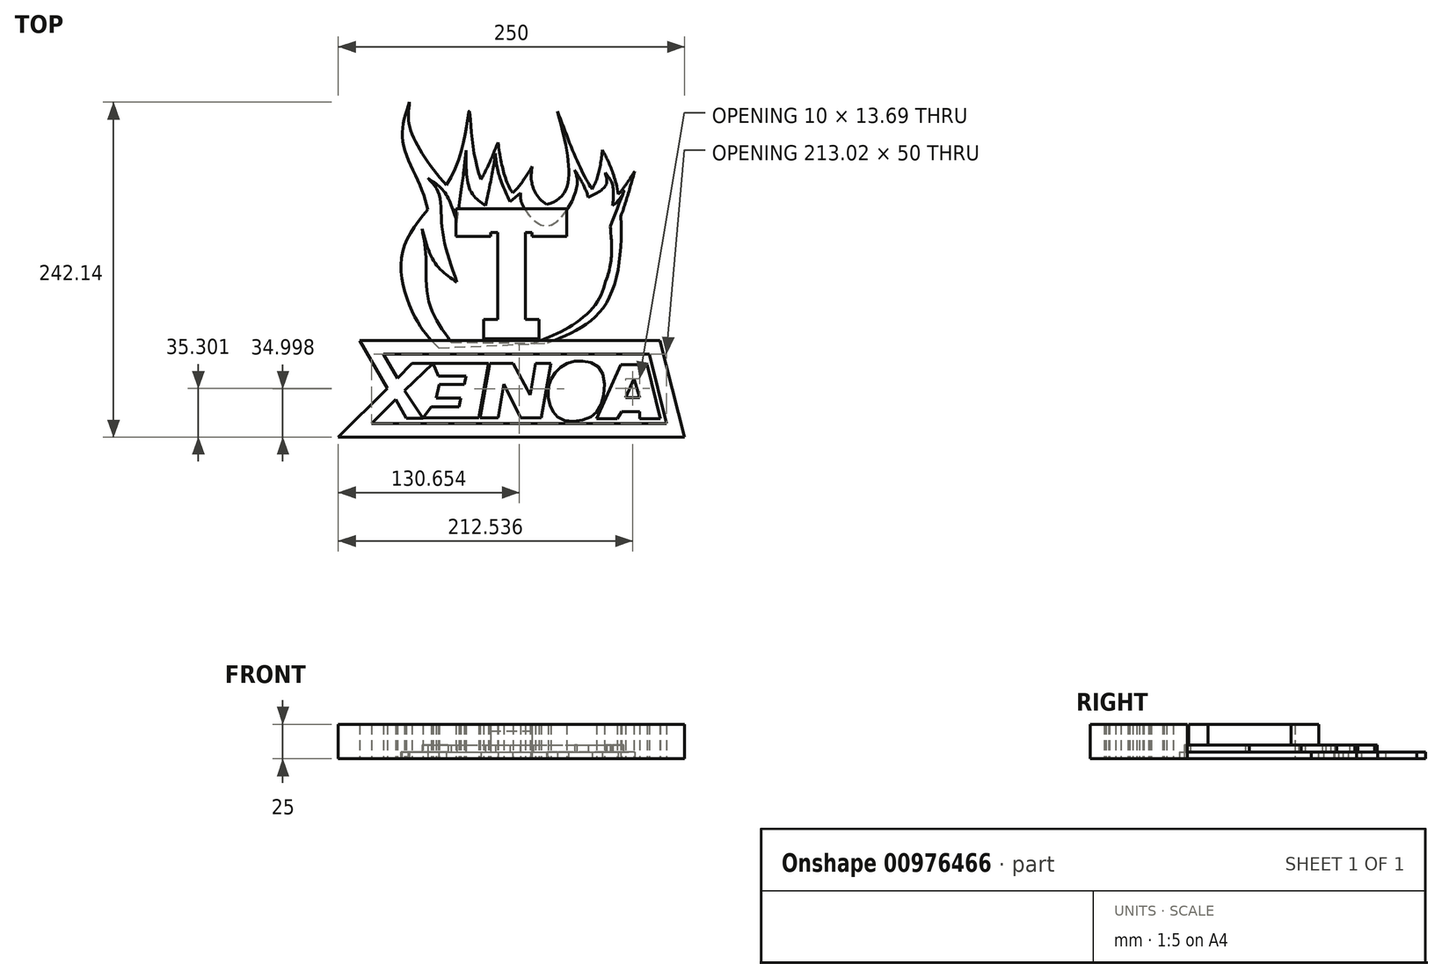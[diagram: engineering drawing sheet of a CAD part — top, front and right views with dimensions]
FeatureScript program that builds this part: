
annotation { "Feature Type Name" : "Feature", "Feature Type Description" : "" }
export const myFeature = defineFeature(function(context is Context, id is Id, definition is map)
    precondition{}
    {
        {
            var Q0;
            Q0=qCreatedBy(makeId("Top.planeOp"),FACE);
            var sketch = newSketch(context, id + "F0", { "sketchPlane" : qUnion([Q0])});
            skLineSegment(sketch, "E0", {"start": v(0, 0) * mm, "end": v(250, 0) * mm});
            skLineSegment(sketch, "E1", {"start": v(0, 0) * mm, "end": v(35.36, 35.36) * mm});
            skLineSegment(sketch, "E2", {"start": v(35.36, 35.36) * mm, "end": v(15.36, 70) * mm});
            skLineSegment(sketch, "E3", {"start": v(15.36, 70) * mm, "end": v(232.36, 70) * mm});
            skLineSegment(sketch, "E4", {"start": v(232.36, 70) * mm, "end": v(250, 0) * mm});
            skLineSegment(sketch, "E5.0", {"start": v(224.56, 60) * mm, "end": v(237.17, 10) * mm});
            skLineSegment(sketch, "E5.1", {"start": v(32.68, 60) * mm, "end": v(224.56, 60) * mm});
            skLineSegment(sketch, "E5.2", {"start": v(24.14, 10) * mm, "end": v(237.17, 10) * mm});
            skLineSegment(sketch, "E5.3", {"start": v(24.14, 10) * mm, "end": v(47.85, 33.71) * mm});
            skLineSegment(sketch, "E5.4", {"start": v(47.85, 33.71) * mm, "end": v(32.68, 60) * mm});
            skLineSegment(sketch, "E6", {"start": v(42.68, 42.68) * mm, "end": v(53.28, 53.28) * mm});
            skLineSegment(sketch, "E7", {"start": v(53.28, 53.28) * mm, "end": v(68.28, 53.28) * mm});
            skLineSegment(sketch, "E8", {"start": v(68.28, 53.28) * mm, "end": v(47.85, 33.71) * mm});
            skLineSegment(sketch, "E9", {"start": v(47.85, 33.71) * mm, "end": v(61.2, 13.76) * mm});
            skLineSegment(sketch, "E10", {"start": v(61.2, 13.76) * mm, "end": v(49.2, 13.76) * mm});
            skLineSegment(sketch, "E11", {"start": v(49.2, 13.76) * mm, "end": v(41.4, 27.26) * mm});
            skLineSegment(sketch, "E12", {"start": v(68.28, 53.28) * mm, "end": v(108.28, 53.28) * mm});
            skLineSegment(sketch, "E13", {"start": v(108.28, 53.28) * mm, "end": v(101.34, 13.9) * mm});
            skLineSegment(sketch, "E14", {"start": v(101.34, 13.9) * mm, "end": v(61.2, 13.9) * mm});
            skLineSegment(sketch, "E15", {"start": v(61.2, 13.9) * mm, "end": v(67.1, 21.96) * mm});
            skLineSegment(sketch, "E16", {"start": v(68.28, 53.28) * mm, "end": v(72.31, 44.13) * mm});
            skLineSegment(sketch, "E17", {"start": v(72.31, 44.13) * mm, "end": v(92.31, 44.13) * mm});
            skLineSegment(sketch, "E18", {"start": v(67.1, 21.96) * mm, "end": v(87.1, 21.96) * mm});
            skLineSegment(sketch, "E19", {"start": v(108.28, 53.28) * mm, "end": v(109.28, 53.28) * mm});
            skLineSegment(sketch, "E20", {"start": v(101.34, 13.9) * mm, "end": v(102.34, 13.9) * mm});
            skLineSegment(sketch, "E21", {"start": v(102.34, 13.9) * mm, "end": v(109.28, 53.28) * mm});
            skLineSegment(sketch, "E22", {"start": v(109.28, 53.28) * mm, "end": v(126.28, 53.28) * mm});
            skLineSegment(sketch, "E23", {"start": v(102.34, 13.9) * mm, "end": v(115.34, 13.9) * mm});
            skLineSegment(sketch, "E24", {"start": v(115.34, 13.9) * mm, "end": v(119.68, 38.51) * mm});
            skLineSegment(sketch, "E25", {"start": v(119.68, 38.51) * mm, "end": v(131.54, 13.92) * mm});
            skLineSegment(sketch, "E26", {"start": v(131.54, 13.92) * mm, "end": v(146.54, 13.92) * mm});
            skLineSegment(sketch, "E27", {"start": v(146.54, 13.92) * mm, "end": v(153.48, 53.31) * mm});
            skLineSegment(sketch, "E28", {"start": v(142.52, 53.31) * mm, "end": v(138.53, 30.66) * mm});
            skLineSegment(sketch, "E29", {"start": v(138.53, 30.66) * mm, "end": v(126.28, 53.28) * mm});
            skLineSegment(sketch, "E30", {"start": v(92.31, 44.13) * mm, "end": v(87.1, 21.96) * mm});
            skPoint(sketch, "E31", {"position": v(89.73, 33.13) * mm});
            skPoint(sketch, "E32", {"position": v(90.9, 38.13) * mm});
            skPoint(sketch, "E33", {"position": v(88.55, 28.13) * mm});
            skLineSegment(sketch, "E34", {"start": v(90.9, 38.13) * mm, "end": v(72.9, 38.13) * mm});
            skLineSegment(sketch, "E35", {"start": v(88.55, 28.13) * mm, "end": v(70.55, 28.13) * mm});
            skLineSegment(sketch, "E36", {"start": v(70.55, 28.13) * mm, "end": v(72.9, 38.13) * mm});
            skPoint(sketch, "E37", {"position": v(150, 33.62) * mm});
            skLineSegment(sketch, "E38", {"start": v(142.52, 53.31) * mm, "end": v(153.48, 53.31) * mm});
            skLineSegment(sketch, "E39", {"start": v(223.08, 52.32) * mm, "end": v(232.54, 13.45) * mm});
            skLineSegment(sketch, "E40", {"start": v(232.54, 13.45) * mm, "end": v(217.54, 13.45) * mm});
            skLineSegment(sketch, "E41", {"start": v(217.54, 13.45) * mm, "end": v(217.54, 18.45) * mm});
            skLineSegment(sketch, "E42", {"start": v(217.54, 18.45) * mm, "end": v(204.54, 18.45) * mm});
            skLineSegment(sketch, "E43", {"start": v(204.54, 18.45) * mm, "end": v(201.54, 13.26) * mm});
            skLineSegment(sketch, "E44", {"start": v(201.54, 13.26) * mm, "end": v(186.54, 13.26) * mm});
            skLineSegment(sketch, "E45", {"start": v(186.54, 13.26) * mm, "end": v(204.08, 52.51) * mm});
            skLineSegment(sketch, "E46", {"start": v(204.08, 52.51) * mm, "end": v(223.08, 52.32) * mm});
            skLineSegment(sketch, "E47", {"start": v(217.54, 18.45) * mm, "end": v(217.54, 28.45) * mm});
            skLineSegment(sketch, "E48", {"start": v(217.54, 28.45) * mm, "end": v(207.54, 28.45) * mm});
            skLineSegment(sketch, "E49", {"start": v(207.54, 28.45) * mm, "end": v(213.66, 42.15) * mm});
            skLineSegment(sketch, "E50", {"start": v(213.66, 42.15) * mm, "end": v(217.54, 28.45) * mm});
            skFitSpline(sketch, "E51", {"points": [v(151.53, 33.62) * mm, v(153.96, 42.44) * mm, v(162.22, 51.87) * mm, v(176.24, 55.02) * mm, v(189.9, 48.28) * mm, v(190.07, 24.56) * mm, v(179.83, 13.34) * mm, v(161.41, 12.8) * mm, v(153.5, 21.42) * mm, v(151.53, 33.62) * mm]});
            skFitSpline(sketch, "E52.0", {"points": [v(161.5, 32.03) * mm, v(161.5, 33.17) * mm, v(161.6, 34.1) * mm, v(161.72, 34.9) * mm, v(161.9, 35.62) * mm, v(162.1, 36.23) * mm, v(162.32, 36.76) * mm, v(162.51, 37.2) * mm, v(162.74, 37.66) * mm, v(163.1, 38.33) * mm, v(163.6, 39.18) * mm, v(164.29, 40.2) * mm, v(165.04, 41.16) * mm, v(165.83, 42.02) * mm, v(166.5, 42.63) * mm, v(167.02, 43.04) * mm, v(167.4, 43.32) * mm, v(167.76, 43.55) * mm, v(168.15, 43.77) * mm, v(168.57, 43.97) * mm, v(169.16, 44.23) * mm, v(169.98, 44.52) * mm, v(171.09, 44.8) * mm, v(172.32, 44.98) * mm, v(173.66, 45.08) * mm, v(174.73, 45.08) * mm, v(175.47, 45.05) * mm, v(175.97, 45.02) * mm, v(176.58, 44.96) * mm, v(177.28, 44.87) * mm, v(178.15, 44.72) * mm, v(179.13, 44.48) * mm, v(180.04, 44.14) * mm, v(180.66, 43.8) * mm, v(180.95, 43.58) * mm, v(181.1, 43.43) * mm, v(181.19, 43.33) * mm, v(181.25, 43.24) * mm, v(181.3, 43.16) * mm, v(181.36, 43.06) * mm, v(181.42, 42.92) * mm, v(181.52, 42.7) * mm, v(181.7, 42.18) * mm, v(181.98, 41.11) * mm, v(182.2, 39.44) * mm, v(182.28, 37.48) * mm, v(182.2, 35.37) * mm, v(181.95, 33.2) * mm, v(181.56, 31.09) * mm, v(181.07, 29.13) * mm, v(180.5, 27.45) * mm, v(179.93, 26.15) * mm, v(179.38, 25.18) * mm, v(178.87, 24.48) * mm, v(178.37, 23.95) * mm, v(177.83, 23.5) * mm, v(177.14, 23.07) * mm, v(176.21, 22.64) * mm, v(174.96, 22.2) * mm, v(173.46, 21.83) * mm, v(171.82, 21.57) * mm, v(170.14, 21.44) * mm, v(168.53, 21.45) * mm, v(167.32, 21.56) * mm, v(166.48, 21.7) * mm, v(165.94, 21.82) * mm, v(165.57, 21.92) * mm, v(165.33, 22) * mm, v(165.17, 22.06) * mm, v(165.05, 22.11) * mm, v(164.9, 22.18) * mm, v(164.74, 22.27) * mm, v(164.57, 22.37) * mm, v(164.38, 22.52) * mm, v(164.13, 22.75) * mm, v(163.8, 23.16) * mm, v(163.4, 23.77) * mm, v(163, 24.6) * mm, v(162.58, 25.68) * mm, v(162.21, 26.88) * mm, v(161.81, 28.59) * mm, v(161.57, 30.37) * mm, v(161.5, 32.03) * mm, v(161.5, 33.17) * mm, v(161.6, 34.1) * mm, v(161.5, 32.03) * mm]});
            skLineSegment(sketch, "E53", {"start": v(179.1, 44.47) * mm, "end": v(162.82, 25.07) * mm});
            skLineSegment(sketch, "E54", {"start": v(181.97, 41) * mm, "end": v(165.9, 21.83) * mm});
            skPoint(sketch, "E55", {"position": v(-91.58, 195.9) * mm});
            skPoint(sketch, "E56", {"position": v(125, 70) * mm});
            skPoint(sketch, "E57", {"position": v(105, 70) * mm});
            skPoint(sketch, "E58", {"position": v(145, 70) * mm});
            skLineSegment(sketch, "E59", {"start": v(105, 70) * mm, "end": v(105, 85) * mm});
            skLineSegment(sketch, "E60", {"start": v(105, 85) * mm, "end": v(145, 85) * mm});
            skLineSegment(sketch, "E61", {"start": v(145, 85) * mm, "end": v(145, 70) * mm});
            skPoint(sketch, "E62", {"position": v(125, 85) * mm});
            skPoint(sketch, "E63", {"position": v(115, 85) * mm});
            skPoint(sketch, "E64", {"position": v(135, 85) * mm});
            skLineSegment(sketch, "E65", {"start": v(115, 85) * mm, "end": v(115, 165) * mm});
            skLineSegment(sketch, "E66", {"start": v(135, 85) * mm, "end": v(135, 165) * mm});
            skLineSegment(sketch, "E67", {"start": v(115, 165) * mm, "end": v(135, 165) * mm});
            skLineSegment(sketch, "E68", {"start": v(115, 165) * mm, "end": v(85, 165) * mm});
            skLineSegment(sketch, "E69", {"start": v(135, 165) * mm, "end": v(165, 165) * mm});
            skLineSegment(sketch, "E70", {"start": v(165, 165) * mm, "end": v(165, 145) * mm});
            skLineSegment(sketch, "E71", {"start": v(165, 145) * mm, "end": v(140, 145) * mm});
            skLineSegment(sketch, "E72", {"start": v(140, 145) * mm, "end": v(140, 148) * mm});
            skLineSegment(sketch, "E73", {"start": v(140, 148) * mm, "end": v(135, 148) * mm});
            skLineSegment(sketch, "E74", {"start": v(85, 165) * mm, "end": v(85, 145) * mm});
            skLineSegment(sketch, "E75", {"start": v(85, 145) * mm, "end": v(110, 145) * mm});
            skLineSegment(sketch, "E76", {"start": v(110, 145) * mm, "end": v(110, 148) * mm});
            skLineSegment(sketch, "E77", {"start": v(110, 148) * mm, "end": v(115, 148) * mm});
            skLineSegment(sketch, "E78", {"start": v(105, 71) * mm, "end": v(145, 71) * mm});
            skSolve(sketch);
        }
        {
            var Q0;
            Q0=makeQuery(id+"F0.imprint","IMPRINT",FACE,{"disambiguationData":[TD([[makeQuery(id+"F0.imprint","IMPRINT",EDGE,{"derivedFrom":sQuery(id+"F0.wireOp",EDGE,"E0")}),1.0]])]});
            var Q1;
            {var subQ2=sQuery(id+"F0.wireOp",EDGE,"E6");Q1=makeQuery(id+"F0.imprint","IMPRINT",FACE,{"disambiguationData":[TD([[makeQuery(id+"F0.imprint","IMPRINT",EDGE,{"derivedFrom":subQ2}),-1.0]])]});}
            var Q2;
            {var subQ0=sQuery(id+"F0.wireOp",EDGE,"E9");Q2=makeQuery(id+"F0.imprint","IMPRINT",FACE,{"disambiguationData":[TD([[makeQuery(id+"F0.imprint","IMPRINT",EDGE,{"derivedFrom":subQ0}),-1.0]])]});}
            var Q3;
            {var subQ0=sQuery(id+"F0.wireOp",EDGE,"E34");Q3=makeQuery(id+"F0.imprint","IMPRINT",FACE,{"disambiguationData":[TD([[makeQuery(id+"F0.imprint","IMPRINT",EDGE,{"derivedFrom":subQ0}),1.0]])]});}
            var Q4;
            Q4=makeQuery(id+"F0.imprint","IMPRINT",FACE,{"disambiguationData":[TD([[makeQuery(id+"F0.imprint","IMPRINT",EDGE,{"derivedFrom":sQuery(id+"F0.wireOp",EDGE,"E12")}),-1.0]])]});
            var Q5;
            Q5=makeQuery(id+"F0.imprint","IMPRINT",FACE,{"disambiguationData":[TD([[makeQuery(id+"F0.imprint","IMPRINT",EDGE,{"derivedFrom":sQuery(id+"F0.wireOp",EDGE,"E21")}),-1.0]])]});
            var Q6;
            Q6=makeQuery(id+"F0.imprint","IMPRINT",FACE,{"disambiguationData":[TD([[makeQuery(id+"F0.imprint","IMPRINT",EDGE,{"derivedFrom":sQuery(id+"F0.wireOp",EDGE,"E51")}),-1.0]])]});
            var Q7;
            {var subQ0=sQuery(id+"F0.wireOp",EDGE,"E53");Q7=makeQuery(id+"F0.imprint","IMPRINT",FACE,{"disambiguationData":[TD([[makeQuery(id+"F0.imprint","IMPRINT",EDGE,{"derivedFrom":subQ0}),1.0]])]});}
            var Q8;
            Q8=makeQuery(id+"F0.imprint","IMPRINT",FACE,{"disambiguationData":[TD([[makeQuery(id+"F0.imprint","IMPRINT",EDGE,{"derivedFrom":sQuery(id+"F0.wireOp",EDGE,"E39")}),-1.0]])]});
            var Q9;
            {var subQ0=sQuery(id+"F0.wireOp",EDGE,"JfNl9Xfk-aqaR-qNYz-ximk-0m5AAW0ROm31");Q9=makeQuery(id+"F0.imprint","IMPRINT",FACE,{"disambiguationData":[TD([[makeQuery(id+"F0.imprint","IMPRINT",EDGE,{"derivedFrom":subQ0}),-1.0]])]});}
            var Q10;
            {var subQ0=sQuery(id+"F0.wireOp",EDGE,"E15");var subQ1=sQuery(id+"F0.wireOp",EDGE,"E14");var subQ2=makeQuery(id+"F0.imprint","INTERSECT",VERTEX,{"derivedFrom":[subQ1,subQ0]});Q10=makeQuery(id+"F0.imprint","IMPRINT",FACE,{"disambiguationData":[TD([[makeQuery(id+"F0.imprint","IMPRINT",EDGE,{"disambiguationData":[TD([[subQ2,1.0]])],"derivedFrom":subQ1}),-1.0]])]});}
            var Q11;
            {var subQ3=sQuery(id+"F0.wireOp",EDGE,"eN30COPq-oqJq-rnKl-EqHf-OhdowSKKRAAw");Q11=makeQuery(id+"F0.imprint","IMPRINT",FACE,{"disambiguationData":[TD([[makeQuery(id+"F0.imprint","IMPRINT",EDGE,{"derivedFrom":subQ3}),1.0]])]});}
            var Q12;
            {var subQ0=sQuery(id+"F0.wireOp",EDGE,"imM2ijot-e2D8-q0Y7-5tzL-eRpiLB6fCpNz");Q12=makeQuery(id+"F0.imprint","IMPRINT",FACE,{"disambiguationData":[TD([[makeQuery(id+"F0.imprint","IMPRINT",EDGE,{"derivedFrom":subQ0}),-1.0]])]});}
            var Q13;
            {var subQ0=sQuery(id+"F0.wireOp",EDGE,"RDafbrLf-kzFO-E4ZM-40qh-3E63GRLbKq8Y");Q13=makeQuery(id+"F0.imprint","IMPRINT",FACE,{"disambiguationData":[TD([[makeQuery(id+"F0.imprint","IMPRINT",EDGE,{"derivedFrom":subQ0}),-1.0]])]});}
            var Q14;
            {var subQ0=sQuery(id+"F0.wireOp",EDGE,"6cAeuiRb-naha-nZBh-ziNz-JyJCdYFGemb1");Q14=makeQuery(id+"F0.imprint","IMPRINT",FACE,{"disambiguationData":[TD([[makeQuery(id+"F0.imprint","IMPRINT",EDGE,{"derivedFrom":subQ0}),-1.0]])]});}
            var Q15;
            {var subQ0=sQuery(id+"F0.wireOp",EDGE,"ylp7s7nb-VYOC-vkmB-fRLy-HwE1BUQnb8ae");Q15=makeQuery(id+"F0.imprint","IMPRINT",FACE,{"disambiguationData":[TD([[makeQuery(id+"F0.imprint","IMPRINT",EDGE,{"derivedFrom":subQ0}),-1.0]])]});}
            var Q16;
            {var subQ0=sQuery(id+"F0.wireOp",EDGE,"D8vqczcZ-tITf-OYWz-xtXg-1sGLX5qLOuWc");Q16=makeQuery(id+"F0.imprint","IMPRINT",FACE,{"disambiguationData":[TD([[makeQuery(id+"F0.imprint","IMPRINT",EDGE,{"derivedFrom":subQ0}),-1.0]])]});}
            var Q17;
            {var subQ0=sQuery(id+"F0.wireOp",EDGE,"E67");Q17=makeQuery(id+"F0.imprint","IMPRINT",FACE,{"disambiguationData":[TD([[makeQuery(id+"F0.imprint","IMPRINT",EDGE,{"derivedFrom":subQ0}),-1.0]])]});}
            var Q18;
            {var subQ0=sQuery(id+"F0.wireOp",EDGE,"E68");Q18=makeQuery(id+"F0.imprint","IMPRINT",FACE,{"disambiguationData":[TD([[makeQuery(id+"F0.imprint","IMPRINT",EDGE,{"derivedFrom":subQ0}),1.0]])]});}
            var Q19;
            {var subQ0=sQuery(id+"F0.wireOp",EDGE,"E69");Q19=makeQuery(id+"F0.imprint","IMPRINT",FACE,{"disambiguationData":[TD([[makeQuery(id+"F0.imprint","IMPRINT",EDGE,{"derivedFrom":subQ0}),-1.0]])]});}
            var Q20;
            {var subQ7=sQuery(id+"F0.wireOp",EDGE,"E78");Q20=makeQuery(id+"F0.imprint","IMPRINT",FACE,{"disambiguationData":[TD([[makeQuery(id+"F0.imprint","IMPRINT",EDGE,{"derivedFrom":subQ7}),1.0]])]});}
            extrude(context, id + "F1", {"entities" : qUnion([Q0, Q1, Q2, Q3, Q4, Q5, Q6, Q7, Q8, Q9, Q10, Q11, Q12, Q13, Q14, Q15, Q16, Q17, Q18, Q19, Q20]), "depth" : 25 * mm, "offsetDistance" : 25 * mm});
        }
        {
            var Q0;
            {var subQ5=sQuery(id+"F0.wireOp",EDGE,"E78");Q0=makeQuery(id+"F0.imprint","IMPRINT",FACE,{"disambiguationData":[TD([[makeQuery(id+"F0.imprint","IMPRINT",EDGE,{"derivedFrom":subQ5}),-1.0]])]});}
            extrude(context, id + "F2", {"entities" : qUnion([Q0]), "depth" : 20 * mm, "offsetDistance" : 25 * mm});
        }
        {
            var Q0;
            Q0=makeQuery(id+"F2.opExtrude","SWEPT_FACE",FACE,{"disambiguationData":[OSD([sQuery(id+"F0.wireOp",EDGE,"E61")])]});
            extrude(context, id + "F3", {"entities" : qUnion([Q0]), "operationType" : NewBodyOperationType.REMOVE, "oppositeDirection" : true, "depth" : 5 * mm, "offsetDistance" : 25 * mm});
        }
        {
            var Q0;
            Q0=makeQuery(id+"F2.opExtrude","CAP_FACE",FACE,{"disambiguationData":[OSD([sQuery(id+"F0.wireOp",EDGE,"E3"),sQuery(id+"F0.wireOp",EDGE,"E59"),sQuery(id+"F0.wireOp",EDGE,"E61"),sQuery(id+"F0.wireOp",EDGE,"E78")])],"isStart":true});
            extrude(context, id + "F4", {"entities" : qUnion([Q0]), "operationType" : NewBodyOperationType.REMOVE, "oppositeDirection" : true, "depth" : 5 * mm, "offsetDistance" : 25 * mm});
        }
        {
            var Q0;
            Q0=makeQuery(id+"F2.opExtrude","SWEPT_FACE",FACE,{"disambiguationData":[OSD([sQuery(id+"F0.wireOp",EDGE,"E59")])]});
            extrude(context, id + "F5", {"entities" : qUnion([Q0]), "operationType" : NewBodyOperationType.REMOVE, "oppositeDirection" : true, "depth" : 5 * mm, "offsetDistance" : 25 * mm});
        }
        {
            var Q0;
            Q0=qCreatedBy(makeId("Top.planeOp"),FACE);
            var sketch = newSketch(context, id + "F6", { "sketchPlane" : qUnion([Q0])});
            skFitSpline(sketch, "E79", {"points": [v(72.63, 64.48) * mm, v(58.11, 81.9) * mm, v(46.5, 134.73) * mm, v(84.24, 193.66) * mm, v(94.4, 235.75) * mm, v(96.72, 214.56) * mm, v(108.04, 177.7) * mm, v(121.1, 173.34) * mm, v(139.98, 195.7) * mm], "startDerivative": vector(-140.53, 134.36) * mm, "endDerivative": vector(159.63, 258.15) * mm});
            skFitSpline(sketch, "E80", {"points": [v(139.98, 195.7) * mm, v(139.98, 182.63) * mm, v(152.46, 167.54) * mm, v(180.04, 175.37) * mm, v(190.78, 207.6) * mm], "startDerivative": vector(-9.56, -66.05) * mm, "endDerivative": vector(15.17, 120.6) * mm});
            skFitSpline(sketch, "E81", {"points": [v(190.78, 207.6) * mm, v(201.8, 177.7) * mm, v(194.55, 98.74) * mm, v(151, 67.97) * mm], "startDerivative": vector(48.97, -93.3) * mm, "endDerivative": vector(-153.43, -61.2) * mm});
            skLineSegment(sketch, "E82", {"start": v(72.63, 64.48) * mm, "end": v(151, 67.97) * mm});
            skFitSpline(sketch, "E83", {"points": [v(67.7, 142.28) * mm, v(61.02, 176.83) * mm, v(46.5, 213.98) * mm, v(51.44, 242.14) * mm], "startDerivative": vector(-10.44, 101.43) * mm, "endDerivative": vector(31.52, 89.92) * mm});
            skFitSpline(sketch, "E84", {"points": [v(51.44, 242.14) * mm, v(51.44, 225.01) * mm, v(67.4, 195.11) * mm, v(91.5, 175.66) * mm, v(115.3, 213.11) * mm], "startDerivative": vector(-11.34, -87.42) * mm, "endDerivative": vector(73.08, 180.07) * mm});
            skFitSpline(sketch, "E85", {"points": [v(115.3, 213.11) * mm, v(131.56, 171.3) * mm, v(161.75, 174.8) * mm, v(158.27, 235.75) * mm], "startDerivative": vector(23.99, -156.04) * mm, "endDerivative": vector(-49.63, 190.81) * mm});
            skFitSpline(sketch, "E86", {"points": [v(158.27, 235.75) * mm, v(193.1, 171.3) * mm, v(214, 192.21) * mm], "startDerivative": vector(57.93, -154.06) * mm, "endDerivative": vector(53.2, 84.72) * mm});
            skFitSpline(sketch, "E87", {"points": [v(214, 192.21) * mm, v(188.75, 130.67) * mm, v(147.52, 111.8) * mm, v(67.7, 142.28) * mm], "startDerivative": vector(-57.4, -206.1) * mm, "endDerivative": vector(-221.83, 116.43) * mm});
            skSolve(sketch);
        }
        {
            var Q0;
            Q0 = qSketchRegion(id + "F6", true);
            extrude(context, id + "F7", {"entities" : qUnion([Q0]), "depth" : 5 * mm, "offsetDistance" : 25 * mm});
        }
        {
            var Q0;
            Q0=makeQuery(id+"F7.opExtrude","CAP_FACE",FACE,{"disambiguationData":[OSD([sQuery(id+"F6.wireOp",EDGE,"E79"),sQuery(id+"F6.wireOp",EDGE,"E80"),sQuery(id+"F6.wireOp",EDGE,"E81"),sQuery(id+"F6.wireOp",EDGE,"E82"),sQuery(id+"F6.wireOp",EDGE,"E83"),sQuery(id+"F6.wireOp",EDGE,"E84"),sQuery(id+"F6.wireOp",EDGE,"E85"),sQuery(id+"F6.wireOp",EDGE,"E86"),sQuery(id+"F6.wireOp",EDGE,"E87")])],"isStart":false});
            var sketch = newSketch(context, id + "F8", { "sketchPlane" : qUnion([Q0])});
            skFitSpline(sketch, "E88", {"points": [v(79.11, 72.24) * mm, v(65.34, 97.95) * mm, v(63.19, 131.46) * mm, v(60.37, 150.54) * mm], "startDerivative": vector(-48.89, 68.4) * mm, "endDerivative": vector(-13.03, 61.54) * mm});
            skFitSpline(sketch, "E89", {"points": [v(60.37, 150.54) * mm, v(70.32, 125.32) * mm, v(85.58, 112.05) * mm], "startDerivative": vector(14.7, -51.92) * mm, "endDerivative": vector(36.26, -24.38) * mm});
            skFitSpline(sketch, "E90", {"points": [v(85.58, 112.05) * mm, v(74.97, 150.54) * mm, v(72.63, 175.92) * mm, v(64.55, 187.36) * mm], "startDerivative": vector(-33.04, 94.27) * mm, "endDerivative": vector(-39.39, 40.25) * mm});
            skFitSpline(sketch, "E91", {"points": [v(64.55, 187.36) * mm, v(76.96, 176.75) * mm, v(85.58, 155.18) * mm], "startDerivative": vector(29.8, -19.54) * mm, "endDerivative": vector(12.77, -44.1) * mm});
            skFitSpline(sketch, "E92", {"points": [v(85.58, 155.18) * mm, v(90.56, 192) * mm, v(92.22, 207.27) * mm], "startDerivative": vector(9.37, 67.04) * mm, "endDerivative": vector(3.47, 34.8) * mm});
            skFitSpline(sketch, "E93", {"points": [v(92.22, 207.27) * mm, v(95.54, 177.9) * mm, v(106.32, 167.46) * mm], "startDerivative": vector(-0.22, -57.64) * mm, "endDerivative": vector(30.12, -19.87) * mm});
            skFitSpline(sketch, "E94", {"points": [v(106.32, 167.46) * mm, v(112.12, 196.15) * mm, v(113.45, 205.28) * mm], "startDerivative": vector(10.78, 51.02) * mm, "endDerivative": vector(2.73, 21.9) * mm});
            skFitSpline(sketch, "E95", {"points": [v(113.45, 205.28) * mm, v(115.3, 192) * mm, v(123.9, 170.21) * mm], "startDerivative": vector(1.97, -29.21) * mm, "endDerivative": vector(18.18, -40.4) * mm});
            skFitSpline(sketch, "E96", {"points": [v(123.9, 170.21) * mm, v(131.7, 176.55) * mm], "startDerivative": vector(7.8, 6.34) * mm, "endDerivative": vector(7.8, 6.34) * mm});
            skFitSpline(sketch, "E97", {"points": [v(131.7, 176.55) * mm, v(132.86, 168.38) * mm, v(151, 152.7) * mm, v(172, 179.57) * mm, v(170.68, 193.17) * mm], "startDerivative": vector(-3.52, -41.01) * mm, "endDerivative": vector(-19.55, 51.74) * mm});
            skFitSpline(sketch, "E98", {"points": [v(170.68, 193.17) * mm, v(176.99, 182.4) * mm, v(180.64, 173.43) * mm], "startDerivative": vector(12.94, -20.53) * mm, "endDerivative": vector(6.83, -18.91) * mm});
            skFitSpline(sketch, "E99", {"points": [v(180.64, 173.43) * mm, v(193.4, 182.4) * mm, v(192.74, 191.18) * mm], "startDerivative": vector(29.19, 14.37) * mm, "endDerivative": vector(-6.67, 21.47) * mm});
            skFitSpline(sketch, "E100", {"points": [v(192.74, 191.18) * mm, v(198.05, 182.4) * mm, v(198.05, 167.46) * mm], "startDerivative": vector(14.37, -17.56) * mm, "endDerivative": vector(-3.2, -29.51) * mm});
            skFitSpline(sketch, "E101", {"points": [v(198.05, 167.46) * mm, v(203.98, 173.43) * mm, v(206.35, 177.9) * mm, v(196.4, 152.2) * mm], "startDerivative": vector(22.94, 18.5) * mm, "endDerivative": vector(-29.99, -76.8) * mm});
            skFitSpline(sketch, "E102", {"points": [v(196.4, 152.2) * mm, v(193.7, 114.77) * mm, v(154.82, 79.58) * mm, v(79.11, 72.24) * mm], "startDerivative": vector(12.8, -136.78) * mm, "endDerivative": vector(-204.45, 5.06) * mm});
            skLineSegment(sketch, "E103", {"start": v(79.11, 72.24) * mm, "end": v(81.46, 68.6) * mm});
            skLineSegment(sketch, "E104", {"start": v(81.46, 68.6) * mm, "end": v(140.89, 67.96) * mm});
            skFitSpline(sketch, "E105", {"points": [v(140.89, 67.96) * mm, v(166.82, 79.64) * mm, v(186.9, 97.56) * mm, v(193.7, 114.77) * mm], "startDerivative": vector(73.55, 27.97) * mm, "endDerivative": vector(16.1, 60.14) * mm});
            skSolve(sketch);
        }
        {
            var Q0;
            Q0=makeQuery(id+"F8.imprint","IMPRINT",FACE,{"disambiguationData":[TD([[makeQuery(id+"F8.imprint","IMPRINT",EDGE,{"derivedFrom":sQuery(id+"F8.wireOp",EDGE,"E88")}),-1.0]])]});
            var Q1;
            {var subQ0=sQuery(id+"F8.wireOp",EDGE,"E103");Q1=makeQuery(id+"F8.imprint","IMPRINT",FACE,{"disambiguationData":[TD([[makeQuery(id+"F8.imprint","IMPRINT",EDGE,{"derivedFrom":subQ0}),1.0]])]});}
            extrude(context, id + "F9", {"entities" : qUnion([Q0, Q1]), "depth" : 5 * mm, "offsetDistance" : 25 * mm});
        }
    });
